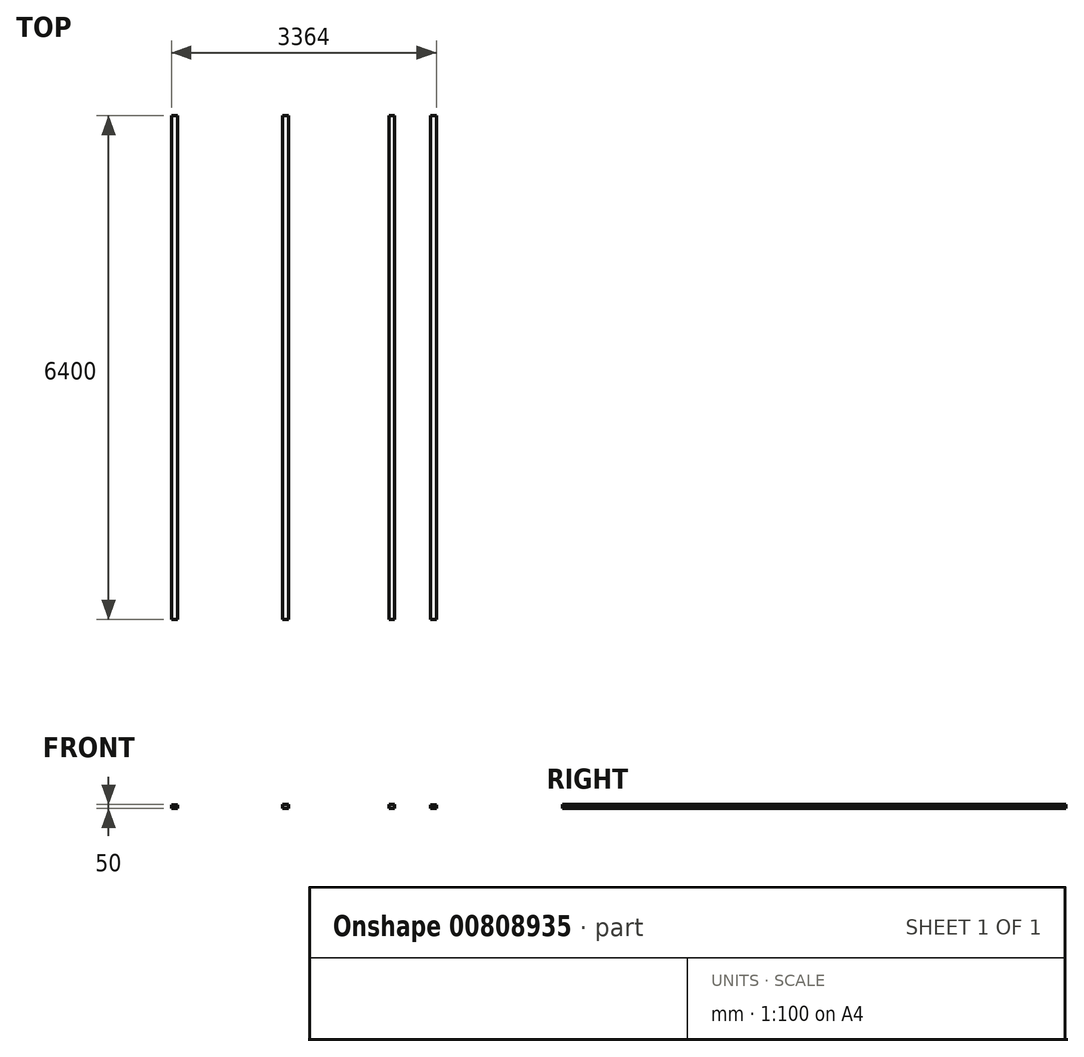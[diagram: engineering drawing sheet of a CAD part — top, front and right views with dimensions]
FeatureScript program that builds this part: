
annotation { "Feature Type Name" : "Feature", "Feature Type Description" : "" }
export const myFeature = defineFeature(function(context is Context, id is Id, definition is map)
    precondition{}
    {
        {
            var Q0;
            Q0=qCreatedBy(makeId("Top.planeOp"),FACE);
            var sketch = newSketch(context, id + "F0", { "sketchPlane" : qUnion([Q0])});
            skLineSegment(sketch, "E0.bottom", {"start": v(0, 0) * mm, "end": v(75, 0) * mm});
            skLineSegment(sketch, "E0.top", {"start": v(0, 6400) * mm, "end": v(75, 6400) * mm});
            skLineSegment(sketch, "E0.left", {"start": v(0, 0) * mm, "end": v(0, 6400) * mm});
            skLineSegment(sketch, "E0.right", {"start": v(75, 0) * mm, "end": v(75, 6400) * mm});
            skLineSegment(sketch, "E1.bottom", {"start": v(1351, 0) * mm, "end": v(1426, 0) * mm});
            skLineSegment(sketch, "E1.top", {"start": v(1351, 6400) * mm, "end": v(1426, 6400) * mm});
            skLineSegment(sketch, "E1.left", {"start": v(1351, 0) * mm, "end": v(1351, 6400) * mm});
            skLineSegment(sketch, "E1.right", {"start": v(1426, 0) * mm, "end": v(1426, 6400) * mm});
            skLineSegment(sketch, "E2.bottom", {"start": v(1879, 0) * mm, "end": v(1954, 0) * mm});
            skLineSegment(sketch, "E2.top", {"start": v(1879, 6400) * mm, "end": v(1954, 6400) * mm});
            skLineSegment(sketch, "E2.left", {"start": v(1879, 0) * mm, "end": v(1879, 6400) * mm});
            skLineSegment(sketch, "E2.right", {"start": v(1954, 0) * mm, "end": v(1954, 6400) * mm});
            skLineSegment(sketch, "E3.bottom", {"start": v(-1410, 6400) * mm, "end": v(-1330, 6400) * mm});
            skLineSegment(sketch, "E3.top", {"start": v(-1410, 0) * mm, "end": v(-1330, 0) * mm});
            skLineSegment(sketch, "E3.left", {"start": v(-1410, 6400) * mm, "end": v(-1410, 0) * mm});
            skLineSegment(sketch, "E3.right", {"start": v(-1330, 6400) * mm, "end": v(-1330, 0) * mm});
            skSolve(sketch);
        }
        {
            var Q0;
            Q0=makeQuery(id+"F0.imprint","IMPRINT",FACE,{"disambiguationData":[TD([[makeQuery(id+"F0.imprint","IMPRINT",EDGE,{"derivedFrom":sQuery(id+"F0.wireOp",EDGE,"E2.bottom")}),1.0]])]});
            extrude(context, id + "F1", {"entities" : qUnion([Q0]), "depth" : 46 * mm, "offsetDistance" : 25 * mm});
        }
        {
            var Q0;
            Q0=makeQuery(id+"F0.imprint","IMPRINT",FACE,{"disambiguationData":[TD([[makeQuery(id+"F0.imprint","IMPRINT",EDGE,{"derivedFrom":sQuery(id+"F0.wireOp",EDGE,"E1.bottom")}),1.0]])]});
            extrude(context, id + "F2", {"entities" : qUnion([Q0]), "depth" : 50 * mm, "offsetDistance" : 25 * mm});
        }
        {
            var Q0;
            Q0=makeQuery(id+"F0.imprint","IMPRINT",FACE,{"disambiguationData":[TD([[makeQuery(id+"F0.imprint","IMPRINT",EDGE,{"derivedFrom":sQuery(id+"F0.wireOp",EDGE,"E0.bottom")}),1.0]])]});
            extrude(context, id + "F3", {"entities" : qUnion([Q0]), "depth" : 50 * mm, "offsetDistance" : 25 * mm});
        }
        {
            var Q0;
            Q0=makeQuery(id+"F0.imprint","IMPRINT",FACE,{"disambiguationData":[TD([[makeQuery(id+"F0.imprint","IMPRINT",EDGE,{"derivedFrom":sQuery(id+"F0.wireOp",EDGE,"E3.bottom")}),-1.0]])]});
            extrude(context, id + "F4", {"entities" : qUnion([Q0]), "depth" : 45 * mm, "offsetDistance" : 25 * mm});
        }
    });
